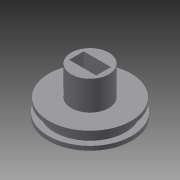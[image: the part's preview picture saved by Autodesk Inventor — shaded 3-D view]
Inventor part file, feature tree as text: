
AUTODESK INVENTOR PART (.ipt)
format: ipt  version: 2015 (Build 190159000, 159)  size: 106,496 bytes
history: native  units: mm
features: sketch x5, extrude x4
ambient origin geometry x8: Origin, YZ Plane, XZ Plane, XY Plane, X Axis, Y Axis, Z Axis, Center Point
bodies: Solid1 (feature_tree)
feature tree (9):
  extrude  "Extrusion1"  Depth=1.0mm TaperAngle=0.0deg
  extrude  "Extrusion2"  Depth=2.0mm TaperAngle=0.0deg
  extrude  "Extrusion3"  Depth=1.0mm
  extrude  "Extrusion4"  Depth=6.5mm
  sketch  "Sketch5"  dims[d11=1.75mm d12=3.25mm d13=7.0mm d14=0.0mm]
  sketch  "Sketch1"  dims[d0=20.0mm d1=1.0mm d2=0.0mm]
  sketch  "Sketch2"  dims[d3=17.0mm d4=2.0mm d5=0.0mm]
  sketch  "Sketch3"  dims[d6=1.0mm d7=0.0mm d8=9.0mm]
  sketch  "Sketch4"  dims[d9=3.5mm d10=6.5mm]
